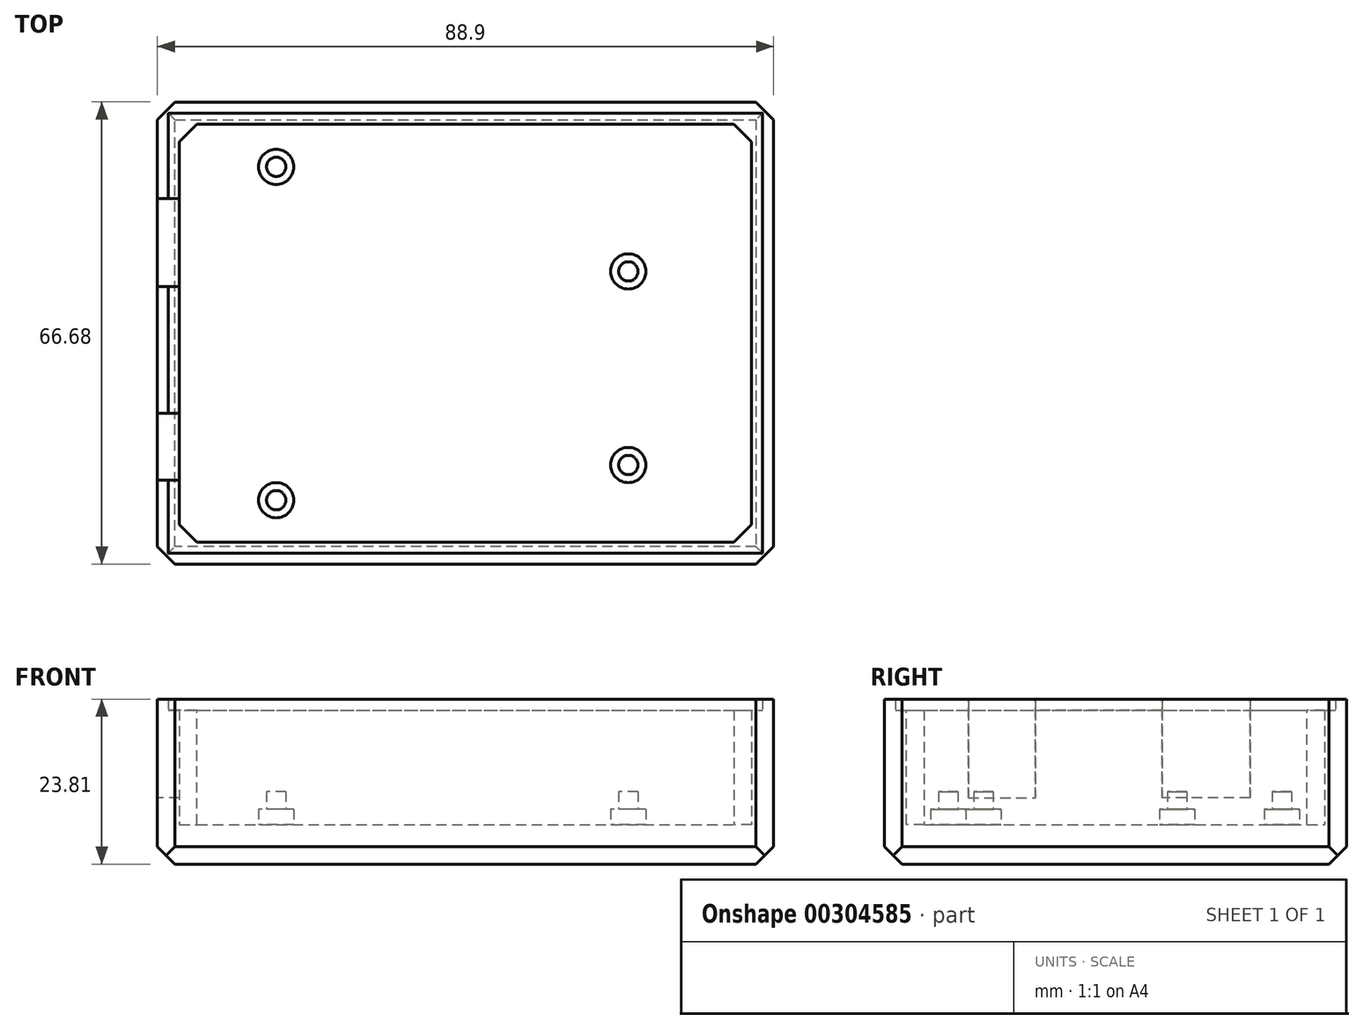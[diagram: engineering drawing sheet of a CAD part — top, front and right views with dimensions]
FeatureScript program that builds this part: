
annotation { "Feature Type Name" : "Feature", "Feature Type Description" : "" }
export const myFeature = defineFeature(function(context is Context, id is Id, definition is map)
    precondition{}
    {
        {
            var Q0;
            Q0=qCreatedBy(makeId("Top.planeOp"),FACE);
            var sketch = newSketch(context, id + "F0", { "sketchPlane" : qUnion([Q0])});
            skLineSegment(sketch, "E0.bottom", {"start": v(0, 0) * mm, "end": v(88.9, 0) * mm});
            skLineSegment(sketch, "E0.top", {"start": v(0, 66.68) * mm, "end": v(88.9, 66.68) * mm});
            skLineSegment(sketch, "E0.left", {"start": v(0, 0) * mm, "end": v(0, 66.68) * mm});
            skLineSegment(sketch, "E0.right", {"start": v(88.9, 0) * mm, "end": v(88.9, 66.68) * mm});
            skSolve(sketch);
        }
        {
            var Q0;
            Q0 = qSketchRegion(id + "F0", true);
            extrude(context, id + "F1", {"entities" : qUnion([Q0]), "depth" : 3.17 * mm});
        }
        {
            var Q0;
            Q0=makeQuery(id+"F1.opExtrude","CAP_FACE",FACE,{"disambiguationData":[OSD([sQuery(id+"F0.wireOp",EDGE,"E0.bottom"),sQuery(id+"F0.wireOp",EDGE,"E0.top"),sQuery(id+"F0.wireOp",EDGE,"E0.left"),sQuery(id+"F0.wireOp",EDGE,"E0.right")])],"isStart":false});
            var sketch = newSketch(context, id + "F2", { "sketchPlane" : qUnion([Q0])});
            skLineSegment(sketch, "E1.bottom", {"start": v(0, 0) * mm, "end": v(88.9, 0) * mm});
            skLineSegment(sketch, "E1.top", {"start": v(0, 66.68) * mm, "end": v(88.9, 66.68) * mm});
            skLineSegment(sketch, "E1.left", {"start": v(0, 0) * mm, "end": v(0, 66.68) * mm});
            skLineSegment(sketch, "E1.right", {"start": v(88.9, 0) * mm, "end": v(88.9, 66.68) * mm});
            skLineSegment(sketch, "E2.0", {"start": v(3.17, 3.18) * mm, "end": v(3.17, 63.5) * mm});
            skLineSegment(sketch, "E2.1", {"start": v(3.18, 3.18) * mm, "end": v(85.73, 3.18) * mm});
            skLineSegment(sketch, "E2.2", {"start": v(85.73, 3.18) * mm, "end": v(85.73, 63.5) * mm});
            skLineSegment(sketch, "E2.3", {"start": v(3.17, 63.5) * mm, "end": v(85.72, 63.5) * mm});
            skSolve(sketch);
        }
        {
            var Q0;
            Q0=makeQuery(id+"F2.imprint","IMPRINT",FACE,{"disambiguationData":[TD([[makeQuery(id+"F2.imprint","IMPRINT",EDGE,{"derivedFrom":sQuery(id+"F2.wireOp",EDGE,"E1.bottom")}),1.0]])]});
            extrude(context, id + "F3", {"entities" : qUnion([Q0]), "operationType" : NewBodyOperationType.ADD, "depth" : 19.05 * mm});
        }
        {
            var Q0;
            Q0=makeQuery(id+"F1.opExtrude","CAP_FACE",FACE,{"disambiguationData":[OSD([sQuery(id+"F0.wireOp",EDGE,"E0.bottom"),sQuery(id+"F0.wireOp",EDGE,"E0.top"),sQuery(id+"F0.wireOp",EDGE,"E0.left"),sQuery(id+"F0.wireOp",EDGE,"E0.right")])],"isStart":false});
            var sketch = newSketch(context, id + "F4", { "sketchPlane" : qUnion([Q0])});
            skCircle(sketch, "E3", {"center": v(17.14, 57.32) * mm, "radius": 2.54 * mm});
            skCircle(sketch, "E4", {"center": v(17.14, 9.2) * mm, "radius": 2.54 * mm});
            skCircle(sketch, "E5", {"center": v(67.95, 42.23) * mm, "radius": 2.54 * mm});
            skCircle(sketch, "E6", {"center": v(67.95, 14.29) * mm, "radius": 2.54 * mm});
            skSolve(sketch);
        }
        {
            var Q0;
            Q0 = qSketchRegion(id + "F4", true);
            extrude(context, id + "F5", {"entities" : qUnion([Q0]), "operationType" : NewBodyOperationType.ADD, "depth" : 4.76 * mm});
        }
        {
            var Q0;
            Q0=makeQuery(id+"F5.opExtrude","CAP_FACE",FACE,{"disambiguationData":[OSD([sQuery(id+"F4.wireOp",EDGE,"E3")])],"isStart":false});
            var sketch = newSketch(context, id + "F6", { "sketchPlane" : qUnion([Q0])});
            skCircle(sketch, "E7", {"center": v(17.14, 57.32) * mm, "radius": 1.4 * mm});
            skSolve(sketch);
        }
        {
            var Q0;
            Q0=makeQuery(id+"F5.opExtrude","CAP_FACE",FACE,{"disambiguationData":[OSD([sQuery(id+"F4.wireOp",EDGE,"E5")])],"isStart":false});
            var sketch = newSketch(context, id + "F7", { "sketchPlane" : qUnion([Q0])});
            skCircle(sketch, "E8", {"center": v(67.95, 42.23) * mm, "radius": 1.4 * mm});
            skSolve(sketch);
        }
        {
            var Q0;
            Q0=makeQuery(id+"F5.opExtrude","CAP_FACE",FACE,{"disambiguationData":[OSD([sQuery(id+"F4.wireOp",EDGE,"E4")])],"isStart":false});
            var sketch = newSketch(context, id + "F8", { "sketchPlane" : qUnion([Q0])});
            skCircle(sketch, "E9", {"center": v(17.14, 9.2) * mm, "radius": 1.4 * mm});
            skSolve(sketch);
        }
        {
            var Q0;
            Q0=makeQuery(id+"F5.opExtrude","CAP_FACE",FACE,{"disambiguationData":[OSD([sQuery(id+"F4.wireOp",EDGE,"E6")])],"isStart":false});
            var sketch = newSketch(context, id + "F9", { "sketchPlane" : qUnion([Q0])});
            skCircle(sketch, "E10", {"center": v(67.95, 14.29) * mm, "radius": 1.4 * mm});
            skSolve(sketch);
        }
        {
            var Q0;
            Q0=makeQuery(id+"F6.imprint","IMPRINT",FACE,{"disambiguationData":[TD([[makeQuery(id+"F6.imprint","IMPRINT",EDGE,{"derivedFrom":sQuery(id+"F6.wireOp",EDGE,"E7")}),1.0]])]});
            var Q1;
            Q1=makeQuery(id+"F1.opExtrude","CAP_FACE",FACE,{"disambiguationData":[OSD([sQuery(id+"F0.wireOp",EDGE,"E0.bottom"),sQuery(id+"F0.wireOp",EDGE,"E0.top"),sQuery(id+"F0.wireOp",EDGE,"E0.left"),sQuery(id+"F0.wireOp",EDGE,"E0.right")])],"isStart":false});
            var Q2;
            Q2=sQuery(id+"F6.wireOp",EDGE,"E7");
            extrude(context, id + "F10", {"entities" : qUnion([Q0, Q1]), "operationType" : NewBodyOperationType.ADD, "surfaceEntities" : qUnion([Q2]), "depth" : 2.54 * mm});
        }
        {
            var Q0;
            Q0=makeQuery(id+"F7.imprint","IMPRINT",FACE,{"disambiguationData":[TD([[makeQuery(id+"F7.imprint","IMPRINT",EDGE,{"derivedFrom":sQuery(id+"F7.wireOp",EDGE,"E8")}),1.0]])]});
            extrude(context, id + "F11", {"entities" : qUnion([Q0]), "operationType" : NewBodyOperationType.ADD, "depth" : 2.54 * mm});
        }
        {
            var Q0;
            Q0=makeQuery(id+"F8.imprint","IMPRINT",FACE,{"disambiguationData":[TD([[makeQuery(id+"F8.imprint","IMPRINT",EDGE,{"derivedFrom":sQuery(id+"F8.wireOp",EDGE,"E9")}),1.0]])]});
            var Q1;
            Q1=sQuery(id+"F8.wireOp",EDGE,"E9");
            extrude(context, id + "F12", {"entities" : qUnion([Q0]), "operationType" : NewBodyOperationType.ADD, "surfaceEntities" : qUnion([Q1]), "depth" : 2.54 * mm});
        }
        {
            var Q0;
            Q0=makeQuery(id+"F9.imprint","IMPRINT",FACE,{"disambiguationData":[TD([[makeQuery(id+"F9.imprint","IMPRINT",EDGE,{"derivedFrom":sQuery(id+"F9.wireOp",EDGE,"E10")}),1.0]])]});
            var Q1;
            Q1=sQuery(id+"F9.wireOp",EDGE,"E10");
            extrude(context, id + "F13", {"entities" : qUnion([Q0]), "operationType" : NewBodyOperationType.ADD, "surfaceEntities" : qUnion([Q1]), "depth" : 2.54 * mm});
        }
        {
            var Q0;
            Q0=makeQuery(id+"F3.boolean.opBoolean","MERGE",FACE,{"derivedFrom":[makeQuery(id+"F1.opExtrude","SWEPT_FACE",FACE,{"disambiguationData":[OSD([sQuery(id+"F0.wireOp",EDGE,"E0.left")])]}),makeQuery(id+"F3.opExtrude","SWEPT_FACE",FACE,{"disambiguationData":[OSD([sQuery(id+"F2.wireOp",EDGE,"E1.left")])]})]});
            var sketch = newSketch(context, id + "F14", { "sketchPlane" : qUnion([Q0])});
            skLineSegment(sketch, "E11.bottom", {"start": v(-52.73, 9.59) * mm, "end": v(-40.03, 9.59) * mm});
            skLineSegment(sketch, "E11.top", {"start": v(-52.73, 22.23) * mm, "end": v(-40.03, 22.23) * mm});
            skLineSegment(sketch, "E11.left", {"start": v(-52.73, 9.59) * mm, "end": v(-52.73, 22.23) * mm});
            skLineSegment(sketch, "E11.right", {"start": v(-40.03, 9.59) * mm, "end": v(-40.03, 22.23) * mm});
            skLineSegment(sketch, "E12.bottom", {"start": v(-12.1, 9.59) * mm, "end": v(-21.75, 9.59) * mm});
            skLineSegment(sketch, "E12.top", {"start": v(-12.1, 22.23) * mm, "end": v(-21.75, 22.23) * mm});
            skLineSegment(sketch, "E12.left", {"start": v(-12.1, 9.59) * mm, "end": v(-12.1, 22.23) * mm});
            skLineSegment(sketch, "E12.right", {"start": v(-21.75, 9.59) * mm, "end": v(-21.75, 22.23) * mm});
            skSolve(sketch);
        }
        {
            var Q0;
            Q0=makeQuery(id+"F14.imprint","IMPRINT",FACE,{"disambiguationData":[TD([[makeQuery(id+"F14.imprint","IMPRINT",EDGE,{"derivedFrom":sQuery(id+"F14.wireOp",EDGE,"E12.bottom")}),-1.0]])]});
            extrude(context, id + "F15", {"entities" : qUnion([Q0]), "operationType" : NewBodyOperationType.REMOVE, "endBound" : BoundingType.UP_TO_NEXT, "oppositeDirection" : true, "depth" : 25.4 * mm});
        }
        {
            var Q0;
            Q0=makeQuery(id+"F14.imprint","IMPRINT",FACE,{"disambiguationData":[TD([[makeQuery(id+"F14.imprint","IMPRINT",EDGE,{"derivedFrom":sQuery(id+"F14.wireOp",EDGE,"E11.bottom")}),1.0]])]});
            extrude(context, id + "F16", {"entities" : qUnion([Q0]), "operationType" : NewBodyOperationType.REMOVE, "endBound" : BoundingType.UP_TO_NEXT, "oppositeDirection" : true, "depth" : 25.4 * mm});
        }
        {
            var Q0;
            {var subQ0=sQuery(id+"F2.wireOp",EDGE,"E2.1");var subQ1=sQuery(id+"F2.wireOp",EDGE,"E2.0");var subQ2=sQuery(id+"F2.wireOp",EDGE,"E1.right");var subQ3=sQuery(id+"F2.wireOp",EDGE,"E1.bottom");var subQ4=sQuery(id+"F2.wireOp",EDGE,"E1.left");var subQ5=sQuery(id+"F2.wireOp",EDGE,"E1.top");var subQ6=sQuery(id+"F2.wireOp",EDGE,"E2.2");var subQ7=sQuery(id+"F2.wireOp",EDGE,"E2.3");Q0=makeQuery(id+"F16.boolean.opBoolean","SPLIT",FACE,{"disambiguationData":[TD([makeQuery(id+"F1.opExtrude","SWEPT_FACE",FACE,{"disambiguationData":[OSD([sQuery(id+"F0.wireOp",EDGE,"E0.bottom")])]})])],"derivedFrom":makeQuery(id+"F3.opExtrude","CAP_FACE",FACE,{"disambiguationData":[OSD([subQ3,subQ5,subQ4,subQ2,subQ1,subQ0,subQ6,subQ7])],"isStart":false})});}
            var sketch = newSketch(context, id + "F17", { "sketchPlane" : qUnion([Q0])});
            skLineSegment(sketch, "E13.0", {"start": v(1.59, 1.59) * mm, "end": v(1.59, 12.1) * mm});
            skLineSegment(sketch, "E13.1", {"start": v(1.59, 52.73) * mm, "end": v(1.59, 65.09) * mm});
            skLineSegment(sketch, "E13.2", {"start": v(1.59, 65.09) * mm, "end": v(87.31, 65.09) * mm});
            skLineSegment(sketch, "E13.3", {"start": v(87.31, 1.59) * mm, "end": v(87.31, 65.09) * mm});
            skLineSegment(sketch, "E13.4", {"start": v(1.59, 1.59) * mm, "end": v(87.31, 1.59) * mm});
            skLineSegment(sketch, "E14", {"start": v(1.59, 52.73) * mm, "end": v(0, 52.73) * mm});
            skLineSegment(sketch, "E15", {"start": v(1.59, 12.1) * mm, "end": v(0, 12.1) * mm});
            skSolve(sketch);
        }
        {
            var Q0;
            Q0=makeQuery(id+"F17.imprint","IMPRINT",FACE,{"disambiguationData":[TD([[makeQuery(id+"F17.imprint","IMPRINT",EDGE,{"derivedFrom":sQuery(id+"F17.wireOp",EDGE,"E13.0")}),1.0]])]});
            extrude(context, id + "F18", {"entities" : qUnion([Q0]), "operationType" : NewBodyOperationType.ADD, "depth" : 1.59 * mm});
        }
        {
            var Q0;
            {var subQ0=sQuery(id+"F2.wireOp",EDGE,"E1.left");var subQ1=sQuery(id+"F2.wireOp",EDGE,"E2.0");Q0=makeQuery(id+"F16.boolean.opBoolean","SPLIT",FACE,{"disambiguationData":[TD([makeQuery(id+"F15.boolean.opBoolean","COPY",FACE,{"derivedFrom":makeQuery(id+"F15.opExtrude","SWEPT_FACE",FACE,{"disambiguationData":[OSD([sQuery(id+"F14.wireOp",EDGE,"E12.right")])]})})])],"derivedFrom":makeQuery(id+"F3.opExtrude","CAP_FACE",FACE,{"disambiguationData":[OSD([sQuery(id+"F2.wireOp",EDGE,"E1.bottom"),sQuery(id+"F2.wireOp",EDGE,"E1.top"),subQ0,sQuery(id+"F2.wireOp",EDGE,"E1.right"),subQ1,sQuery(id+"F2.wireOp",EDGE,"E2.1"),sQuery(id+"F2.wireOp",EDGE,"E2.2"),sQuery(id+"F2.wireOp",EDGE,"E2.3")])],"isStart":false})});}
            var sketch = newSketch(context, id + "F19", { "sketchPlane" : qUnion([Q0])});
            skLineSegment(sketch, "E16.bottom", {"start": v(0, 40.03) * mm, "end": v(1.59, 40.03) * mm});
            skLineSegment(sketch, "E16.top", {"start": v(0, 21.75) * mm, "end": v(1.59, 21.75) * mm});
            skLineSegment(sketch, "E17", {"start": v(0, 40.03) * mm, "end": v(0, 21.75) * mm});
            skLineSegment(sketch, "E18", {"start": v(1.59, 40.03) * mm, "end": v(1.59, 21.75) * mm});
            skSolve(sketch);
        }
        {
            var Q0;
            Q0=makeQuery(id+"F19.imprint","IMPRINT",FACE,{"disambiguationData":[TD([[makeQuery(id+"F19.imprint","IMPRINT",EDGE,{"derivedFrom":sQuery(id+"F19.wireOp",EDGE,"E16.bottom")}),1.0]])]});
            extrude(context, id + "F20", {"entities" : qUnion([Q0]), "operationType" : NewBodyOperationType.ADD, "depth" : 1.59 * mm});
        }
        {
            var Q0;
            {var subQ0=sQuery(id+"F2.wireOp",EDGE,"E1.right");var subQ1=sQuery(id+"F2.wireOp",EDGE,"E1.bottom");Q0=makeQuery(id+"F18.boolean.opBoolean","MERGE",EDGE,{"derivedFrom":[makeQuery(id+"F3.boolean.opBoolean","MERGE",EDGE,{"derivedFrom":[makeQuery(id+"F1.opExtrude","SWEPT_EDGE",EDGE,{"disambiguationData":[OSD([sQuery(id+"F0.wireOp",EDGE,"E0.bottom"),sQuery(id+"F0.wireOp",EDGE,"E0.right")])]}),makeQuery(id+"F3.opExtrude","SWEPT_EDGE",EDGE,{"disambiguationData":[OSD([subQ1,subQ0])]})]}),makeQuery(id+"F18.opExtrude","SWEPT_EDGE",EDGE,{"disambiguationData":[OSD([subQ1,subQ0])]})]});}
            var Q1;
            {var subQ0=sQuery(id+"F2.wireOp",EDGE,"E1.left");var subQ1=sQuery(id+"F2.wireOp",EDGE,"E1.bottom");Q1=makeQuery(id+"F18.boolean.opBoolean","MERGE",EDGE,{"derivedFrom":[makeQuery(id+"F3.boolean.opBoolean","MERGE",EDGE,{"derivedFrom":[makeQuery(id+"F1.opExtrude","SWEPT_EDGE",EDGE,{"disambiguationData":[OSD([sQuery(id+"F0.wireOp",EDGE,"E0.bottom"),sQuery(id+"F0.wireOp",EDGE,"E0.left")])]}),makeQuery(id+"F3.opExtrude","SWEPT_EDGE",EDGE,{"disambiguationData":[OSD([subQ1,subQ0])]})]}),makeQuery(id+"F18.opExtrude","SWEPT_EDGE",EDGE,{"disambiguationData":[OSD([subQ1,subQ0])]})]});}
            var Q2;
            {var subQ0=sQuery(id+"F2.wireOp",EDGE,"E1.right");var subQ1=sQuery(id+"F2.wireOp",EDGE,"E1.top");Q2=makeQuery(id+"F18.boolean.opBoolean","MERGE",EDGE,{"derivedFrom":[makeQuery(id+"F3.boolean.opBoolean","MERGE",EDGE,{"derivedFrom":[makeQuery(id+"F1.opExtrude","SWEPT_EDGE",EDGE,{"disambiguationData":[OSD([sQuery(id+"F0.wireOp",EDGE,"E0.top"),sQuery(id+"F0.wireOp",EDGE,"E0.right")])]}),makeQuery(id+"F3.opExtrude","SWEPT_EDGE",EDGE,{"disambiguationData":[OSD([subQ1,subQ0])]})]}),makeQuery(id+"F18.opExtrude","SWEPT_EDGE",EDGE,{"disambiguationData":[OSD([subQ1,subQ0])]})]});}
            var Q3;
            {var subQ0=sQuery(id+"F2.wireOp",EDGE,"E1.left");var subQ1=sQuery(id+"F2.wireOp",EDGE,"E1.top");Q3=makeQuery(id+"F18.boolean.opBoolean","MERGE",EDGE,{"derivedFrom":[makeQuery(id+"F3.boolean.opBoolean","MERGE",EDGE,{"derivedFrom":[makeQuery(id+"F1.opExtrude","SWEPT_EDGE",EDGE,{"disambiguationData":[OSD([sQuery(id+"F0.wireOp",EDGE,"E0.top"),sQuery(id+"F0.wireOp",EDGE,"E0.left")])]}),makeQuery(id+"F3.opExtrude","SWEPT_EDGE",EDGE,{"disambiguationData":[OSD([subQ1,subQ0])]})]}),makeQuery(id+"F18.opExtrude","SWEPT_EDGE",EDGE,{"disambiguationData":[OSD([subQ1,subQ0])]})]});}
            chamfer(context, id + "F21", {"entities" : qUnion([Q0, Q1, Q2, Q3]), "width" : 2.54 * mm, "tangentPropagation" : true});
        }
        {
            var Q0;
            Q0=makeQuery(id+"F3.opExtrude","SWEPT_EDGE",EDGE,{"disambiguationData":[OSD([sQuery(id+"F2.wireOp",EDGE,"E2.0"),sQuery(id+"F2.wireOp",EDGE,"E2.3")])]});
            var Q1;
            Q1=makeQuery(id+"F3.opExtrude","SWEPT_EDGE",EDGE,{"disambiguationData":[OSD([sQuery(id+"F2.wireOp",EDGE,"E2.2"),sQuery(id+"F2.wireOp",EDGE,"E2.3")])]});
            var Q2;
            Q2=makeQuery(id+"F3.opExtrude","SWEPT_EDGE",EDGE,{"disambiguationData":[OSD([sQuery(id+"F2.wireOp",EDGE,"E2.1"),sQuery(id+"F2.wireOp",EDGE,"E2.2")])]});
            var Q3;
            Q3=makeQuery(id+"F3.opExtrude","SWEPT_EDGE",EDGE,{"disambiguationData":[OSD([sQuery(id+"F2.wireOp",EDGE,"E2.0"),sQuery(id+"F2.wireOp",EDGE,"E2.1")])]});
            chamfer(context, id + "F22", {"entities" : qUnion([Q0, Q1, Q2, Q3]), "width" : 2.54 * mm, "tangentPropagation" : true});
        }
        {
            var Q0;
            Q0=makeQuery(id+"F1.opExtrude","CAP_EDGE",EDGE,{"disambiguationData":[OSD([sQuery(id+"F0.wireOp",EDGE,"E0.bottom")])],"isStart":true});
            var Q1;
            Q1=makeQuery(id+"F1.opExtrude","CAP_EDGE",EDGE,{"disambiguationData":[OSD([sQuery(id+"F0.wireOp",EDGE,"E0.right")])],"isStart":true});
            var Q2;
            Q2=makeQuery(id+"F1.opExtrude","CAP_EDGE",EDGE,{"disambiguationData":[OSD([sQuery(id+"F0.wireOp",EDGE,"E0.top")])],"isStart":true});
            var Q3;
            Q3=makeQuery(id+"F1.opExtrude","CAP_EDGE",EDGE,{"disambiguationData":[OSD([sQuery(id+"F0.wireOp",EDGE,"E0.left")])],"isStart":true});
            chamfer(context, id + "F23", {"entities" : qUnion([Q0, Q1, Q2, Q3]), "width" : 2.54 * mm, "tangentPropagation" : true});
        }
    });
